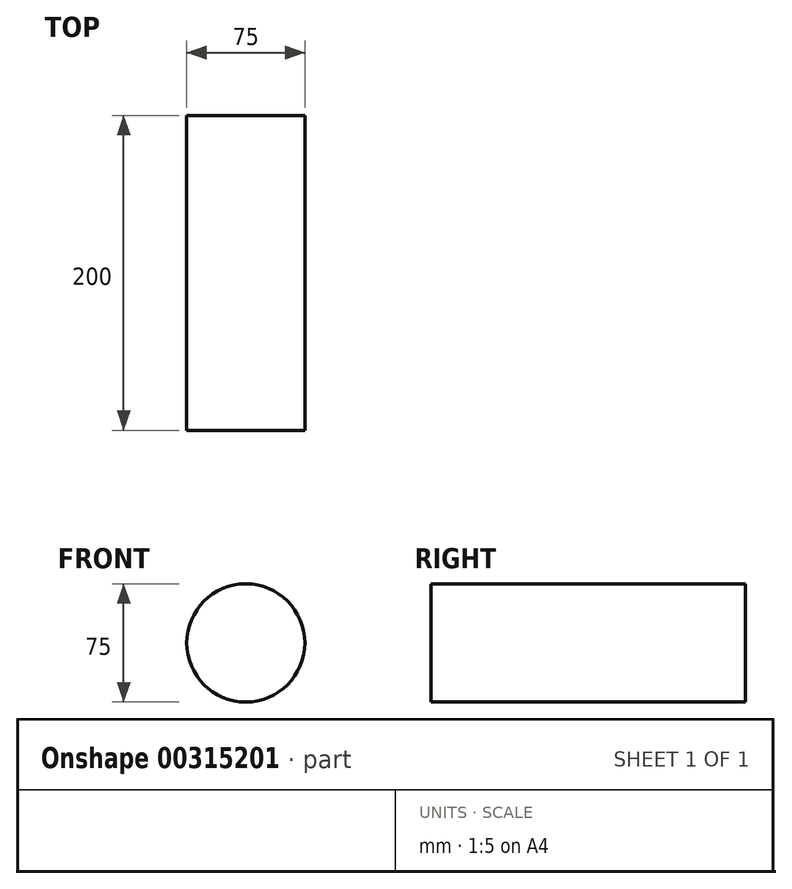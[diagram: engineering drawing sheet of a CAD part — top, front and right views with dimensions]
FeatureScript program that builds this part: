
annotation { "Feature Type Name" : "Feature", "Feature Type Description" : "" }
export const myFeature = defineFeature(function(context is Context, id is Id, definition is map)
    precondition{}
    {
        {
            var Q0;
            Q0=qCreatedBy(makeId("Front.planeOp"),FACE);
            var sketch = newSketch(context, id + "F0", { "sketchPlane" : qUnion([Q0])});
            skCircle(sketch, "E0", {"center": v(0, 0) * mm, "radius": 37.5 * mm});
            skSolve(sketch);
        }
        {
            var Q0;
            Q0=makeQuery(id+"F0.imprint","IMPRINT",FACE,{"disambiguationData":[TD([[makeQuery(id+"F0.imprint","IMPRINT",EDGE,{"derivedFrom":sQuery(id+"F0.wireOp",EDGE,"E0")}),1.0]])]});
            extrude(context, id + "F1", {"entities" : qUnion([Q0]), "depth" : 200 * mm});
        }
    });
